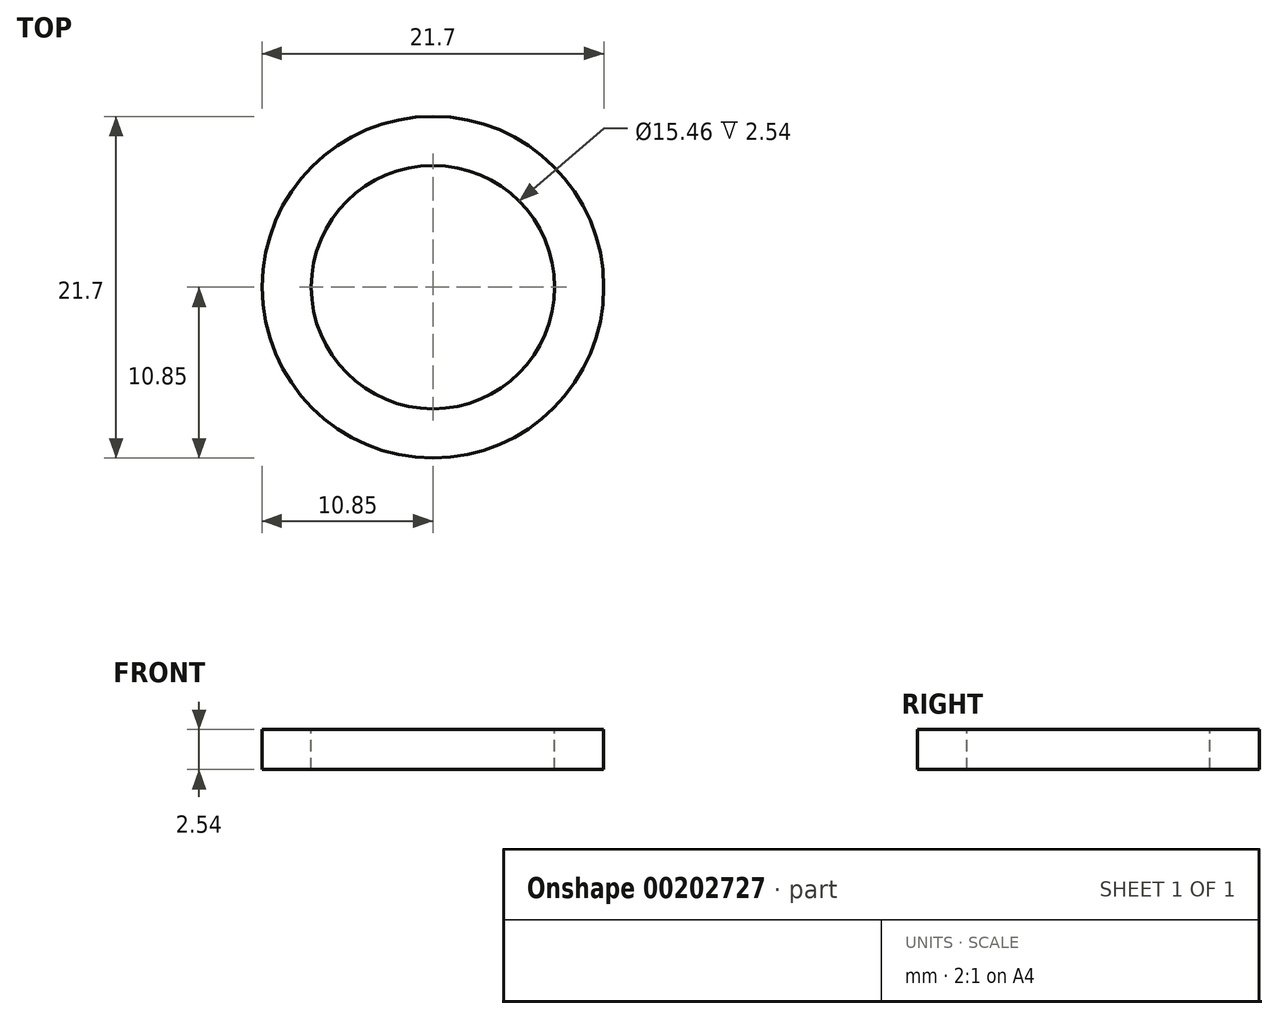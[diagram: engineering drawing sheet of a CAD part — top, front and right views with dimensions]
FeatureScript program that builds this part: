
annotation { "Feature Type Name" : "Feature", "Feature Type Description" : "" }
export const myFeature = defineFeature(function(context is Context, id is Id, definition is map)
    precondition{}
    {
        {
            var Q0;
            Q0=qCreatedBy(makeId("Top.planeOp"),FACE);
            var sketch = newSketch(context, id + "F0", { "sketchPlane" : qUnion([Q0])});
            skCircle(sketch, "E0", {"center": v(0, 0) * mm, "radius": 10.85 * mm});
            skCircle(sketch, "E1", {"center": v(0, 0) * mm, "radius": 7.73 * mm});
            skSolve(sketch);
        }
        {
            var Q0;
            Q0 = qSketchRegion(id + "F0", true);
            var Q1;
            Q1 = qSketchRegion(id + "F2", true);
            extrude(context, id + "F1", {"entities" : qUnion([Q0, Q1]), "oppositeDirection" : true, "depth" : 94.74 * mm});
        }
        {
            var Q0;
            Q0=makeQuery(id+"F1.opExtrude","CAP_FACE",FACE,{"disambiguationData":[OSD([sQuery(id+"F0.wireOp",EDGE,"E0"),sQuery(id+"F0.wireOp",EDGE,"E1")])],"isStart":true});
            var sketch = newSketch(context, id + "F2", { "sketchPlane" : qUnion([Q0])});
            skCircle(sketch, "E2.0", {"center": v(0, 0) * mm, "radius": 7.73 * mm});
            skCircle(sketch, "E3.0", {"center": v(0, 0) * mm, "radius": 10.85 * mm});
            skCircle(sketch, "E4.0", {"center": v(-19.6, 0.63) * mm, "radius": 7.73 * mm});
            skCircle(sketch, "E5.0", {"center": v(-19.6, 0.63) * mm, "radius": 10.85 * mm});
            skSolve(sketch);
        }
        {
            var Q0;
            Q0=makeQuery(id+"F1.opExtrude","SWEPT_FACE",FACE,{"disambiguationData":[OSD([sQuery(id+"F0.wireOp",EDGE,"E0")])]});
            var Q1;
            Q1=makeQuery(id+"F1.opExtrude","CAP_FACE",FACE,{"disambiguationData":[OSD([sQuery(id+"F0.wireOp",EDGE,"E0"),sQuery(id+"F0.wireOp",EDGE,"E1")])],"isStart":true});
            var Q2;
            Q2=makeQuery(id+"F1.opExtrude","SWEPT_FACE",FACE,{"disambiguationData":[OSD([sQuery(id+"F0.wireOp",EDGE,"E1")])]});
            shell(context, id + "F3", {"entities" : qUnion([Q0, Q1, Q2]), "thickness" : 2.54 * mm});
        }
    });
